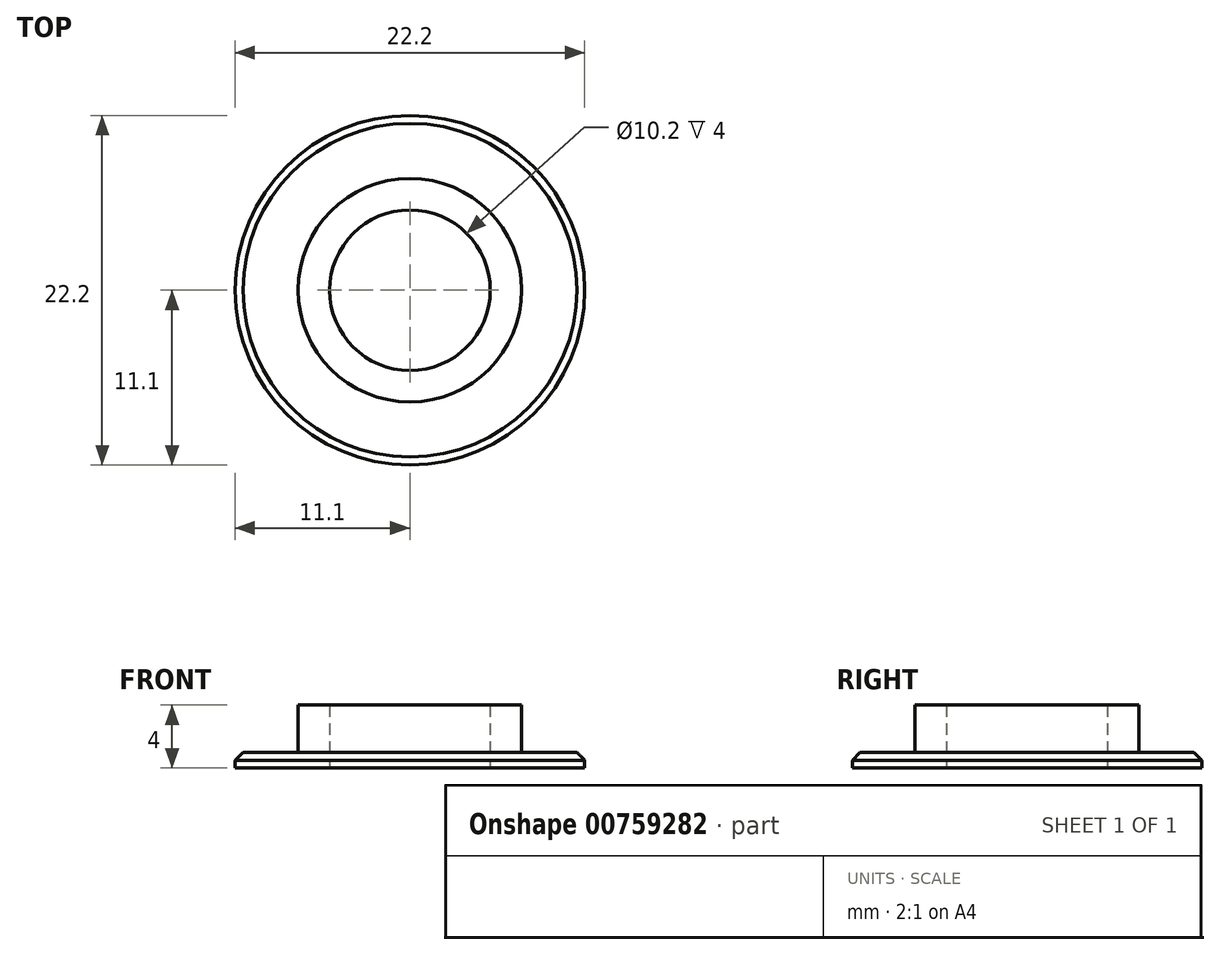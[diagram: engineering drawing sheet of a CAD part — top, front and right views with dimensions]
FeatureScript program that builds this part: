
annotation { "Feature Type Name" : "Feature", "Feature Type Description" : "" }
export const myFeature = defineFeature(function(context is Context, id is Id, definition is map)
    precondition{}
    {
        {
            var Q0;
            Q0=qCreatedBy(makeId("Top.planeOp"),FACE);
            var sketch = newSketch(context, id + "F0", { "sketchPlane" : qUnion([Q0])});
            skCircle(sketch, "E0", {"center": v(0, 0) * mm, "radius": 5.1 * mm});
            skCircle(sketch, "E1", {"center": v(0, 0) * mm, "radius": 11.1 * mm});
            skCircle(sketch, "E2", {"center": v(0, 0) * mm, "radius": 7.1 * mm});
            skCircle(sketch, "E3", {"center": v(0, 0) * mm, "radius": 1.6 * mm});
            skSolve(sketch);
        }
        {
            var Q0;
            Q0=makeQuery(id+"F0.imprint","IMPRINT",FACE,{"disambiguationData":[TD([[makeQuery(id+"F0.imprint","IMPRINT",EDGE,{"derivedFrom":sQuery(id+"F0.wireOp",EDGE,"E0")}),-1.0]])]});
            var Q1;
            Q1=makeQuery(id+"F0.imprint","IMPRINT",FACE,{"disambiguationData":[TD([[makeQuery(id+"F0.imprint","IMPRINT",EDGE,{"derivedFrom":sQuery(id+"F0.wireOp",EDGE,"E0")}),1.0]])]});
            extrude(context, id + "F1", {"entities" : qUnion([Q0, Q1]), "depth" : 4 * mm, "offsetDistance" : 25 * mm});
        }
        {
            var Q0;
            Q0=makeQuery(id+"F0.imprint","IMPRINT",FACE,{"disambiguationData":[TD([[makeQuery(id+"F0.imprint","IMPRINT",EDGE,{"derivedFrom":sQuery(id+"F0.wireOp",EDGE,"E0")}),1.0]])]});
            extrude(context, id + "F2", {"entities" : qUnion([Q0]), "operationType" : NewBodyOperationType.REMOVE, "depth" : 8.2 * mm, "offsetDistance" : 25 * mm});
        }
        {
            var Q0;
            Q0=makeQuery(id+"F0.imprint","IMPRINT",FACE,{"disambiguationData":[TD([[makeQuery(id+"F0.imprint","IMPRINT",EDGE,{"derivedFrom":sQuery(id+"F0.wireOp",EDGE,"E1")}),1.0]])]});
            extrude(context, id + "F3", {"entities" : qUnion([Q0]), "operationType" : NewBodyOperationType.ADD, "depth" : 1 * mm, "offsetDistance" : 25 * mm});
        }
        {
            var Q0;
            Q0=makeQuery(id+"F3.opExtrude","CAP_EDGE",EDGE,{"disambiguationData":[OSD([sQuery(id+"F0.wireOp",EDGE,"E1")])],"isStart":false});
            chamfer(context, id + "F4", {"entities" : qUnion([Q0]), "width" : 0.5 * mm, "tangentPropagation" : true});
        }
    });
